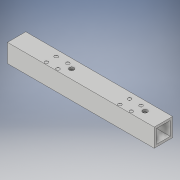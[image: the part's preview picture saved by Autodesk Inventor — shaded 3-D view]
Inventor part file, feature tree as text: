
AUTODESK INVENTOR PART (.ipt)
format: ipt  version: 2018 (Build 220112000, 112)  size: 131,072 bytes
history: native  units: in
note: dims shown in document units (in); Inventor stores cm internally (conversion verified against a paired STEP export)
features: extrude x3, sketch x3
ambient origin geometry x8: Origin, YZ Plane, XZ Plane, XY Plane, X Axis, Y Axis, Z Axis, Center Point
bodies: Solid1 (feature_tree)
feature tree (6):
  extrude  "Extrusion1"  Depth=1.0in
  extrude  "Extrusion2"  Depth=8.0in TaperAngle=0.0deg
  extrude  "Extrusion3"  Depth=0.01in TaperAngle=0.0deg
  sketch  "Sketch1"  dims[d0=1.0in d1=1.0in]
  sketch  "Sketch2"  dims[d2=0.125in d3=8.0in d4=0.0in]
  sketch  "Sketch3"  dims[d9=8.0in d10=0.0in d27=0.01in d28=0.0in d30=2.0in d31=0.25in d32=2.0in d33=0.25in]
